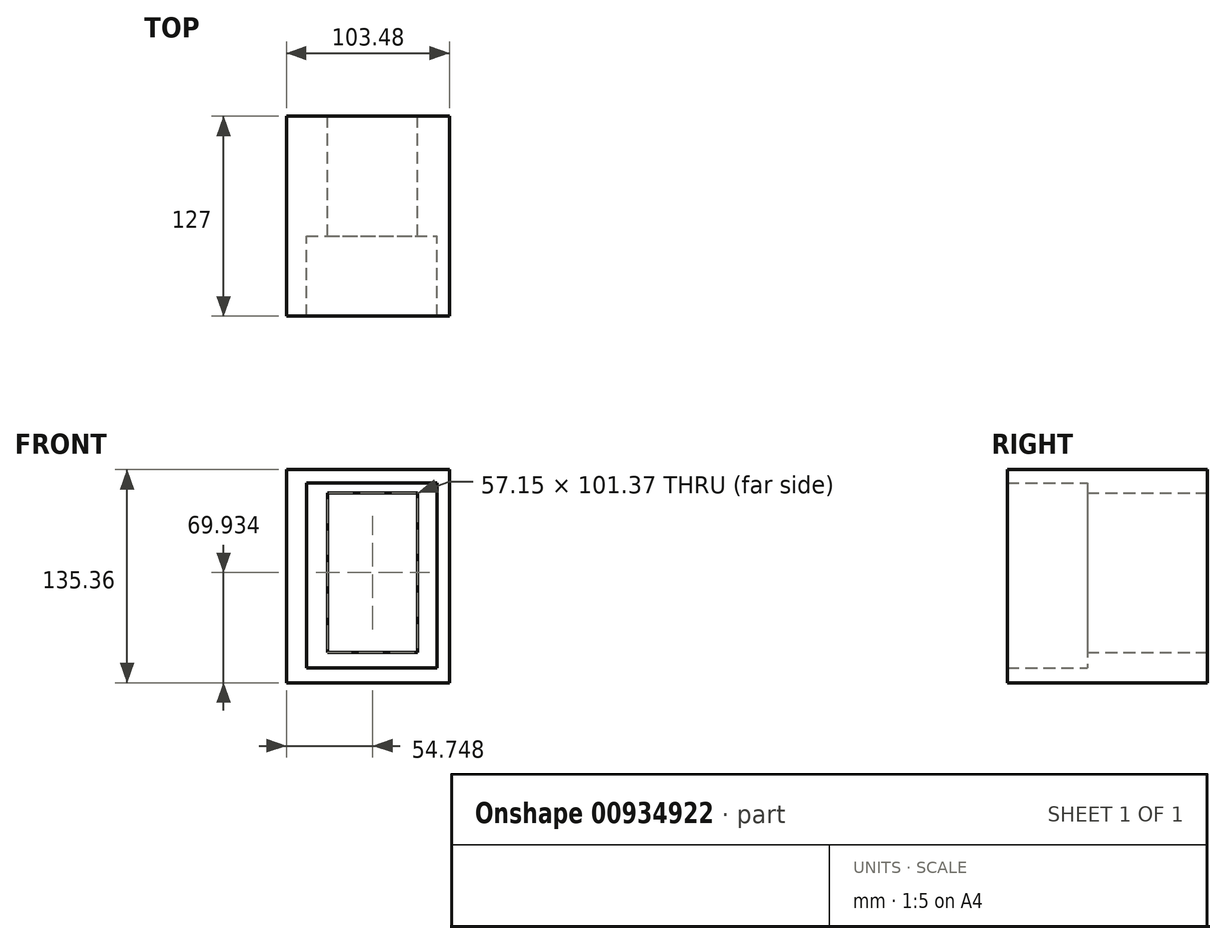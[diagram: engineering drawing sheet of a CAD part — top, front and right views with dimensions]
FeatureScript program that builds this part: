
annotation { "Feature Type Name" : "Feature", "Feature Type Description" : "" }
export const myFeature = defineFeature(function(context is Context, id is Id, definition is map)
    precondition{}
    {
        {
            var Q0;
            Q0=qCreatedBy(makeId("Front.planeOp"),FACE);
            var sketch = newSketch(context, id + "F0", { "sketchPlane" : qUnion([Q0])});
            skLineSegment(sketch, "E0.bottom", {"start": v(-51.59, 66.93) * mm, "end": v(51.89, 66.93) * mm});
            skLineSegment(sketch, "E0.top", {"start": v(-51.59, -68.43) * mm, "end": v(51.89, -68.43) * mm});
            skLineSegment(sketch, "E0.left", {"start": v(-51.59, 66.93) * mm, "end": v(-51.59, -68.43) * mm});
            skLineSegment(sketch, "E0.right", {"start": v(51.89, 66.93) * mm, "end": v(51.89, -68.43) * mm});
            skLineSegment(sketch, "E1.bottom", {"start": v(-38.95, 58.5) * mm, "end": v(44.07, 58.5) * mm});
            skLineSegment(sketch, "E1.top", {"start": v(-38.95, -59.1) * mm, "end": v(44.07, -59.1) * mm});
            skLineSegment(sketch, "E1.left", {"start": v(-38.95, 58.5) * mm, "end": v(-38.95, -59.1) * mm});
            skLineSegment(sketch, "E1.right", {"start": v(44.07, 58.5) * mm, "end": v(44.07, -59.1) * mm});
            skLineSegment(sketch, "E2.bottom", {"start": v(-25.42, 52.19) * mm, "end": v(31.73, 52.19) * mm});
            skLineSegment(sketch, "E2.top", {"start": v(-25.42, -49.18) * mm, "end": v(31.73, -49.18) * mm});
            skLineSegment(sketch, "E2.left", {"start": v(-25.42, 52.19) * mm, "end": v(-25.42, -49.18) * mm});
            skLineSegment(sketch, "E2.right", {"start": v(31.73, 52.19) * mm, "end": v(31.73, -49.18) * mm});
            skSolve(sketch);
        }
        {
            var Q0;
            Q0 = qSketchRegion(id + "F0", true);
            extrude(context, id + "F1", {"entities" : qUnion([Q0]), "depth" : 127 * mm, "offsetDistance" : 25.4 * mm});
        }
        {
            var Q0;
            Q0=makeQuery(id+"F0.imprint","IMPRINT",FACE,{"disambiguationData":[TD([[makeQuery(id+"F0.imprint","IMPRINT",EDGE,{"derivedFrom":sQuery(id+"F0.wireOp",EDGE,"E1.bottom")}),-1.0]])]});
            extrude(context, id + "F2", {"entities" : qUnion([Q0]), "operationType" : NewBodyOperationType.ADD, "depth" : 76.2 * mm, "offsetDistance" : 25.4 * mm});
        }
    });
